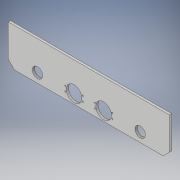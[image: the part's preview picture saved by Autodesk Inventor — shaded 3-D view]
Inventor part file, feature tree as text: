
AUTODESK INVENTOR PART (.ipt)
format: ipt  version: 2017 (Build 210142000, 142)  size: 174,592 bytes
history: native  units: in
note: dims shown in document units (in); Inventor stores cm internally (conversion verified against a paired STEP export)
features: extrude x5, sketch x3, projected_geometry x3, thicken_offset x1
ambient origin geometry x8: Origin, YZ Plane, XZ Plane, XY Plane, X Axis, Y Axis, Z Axis, Center Point
bodies: Solid1 (feature_tree)
feature tree (12):
  extrude  "Extrusion1"  Depth=5.0in
  extrude  "Extrusion2"  Depth=0.25in TaperAngle=0.0deg
  sketch  "Sketch3"  dims[d10=1.124in d14=2.0in d15=0.0in d18=1.124in d19=1.5in d20=180.0deg d31=1.7in d32=1.7in d33=1.0in d34=0.0in d53=0.82in d54=0.82in d55=0.945in d56=0.276in d57=0.138in d58=0.276in d59=0.138in d60=0.945in d61=0.276in d62=0.276in d63=0.138in d64=0.138in d65=0.945in d66=0.945in d67=0.138in d68=0.138in d69=0.138in d70=0.138in d71=1.0in d72=0.0in d73=0.25in d74=7.145in d75=7.145in]
  extrude  "Extrusion3"  Depth=0.25in TaperAngle=0.0deg
  extrude  "Extrusion4"  Depth=0.25in
  thicken_offset  "Thicken1"
  extrude  "Extrusion6"  Depth=0.25in
  sketch  "Sketch1"  dims[d0=17.5in d1=5.0in]
  sketch  "Sketch2"  dims[d2=0.25in d3=0.0in d4=2.0in d5=0.0in]
  projected_geometry  "Projected Loop1"
  projected_geometry  "Projected Loop2"
  projected_geometry  "Project Cut Edges1"
